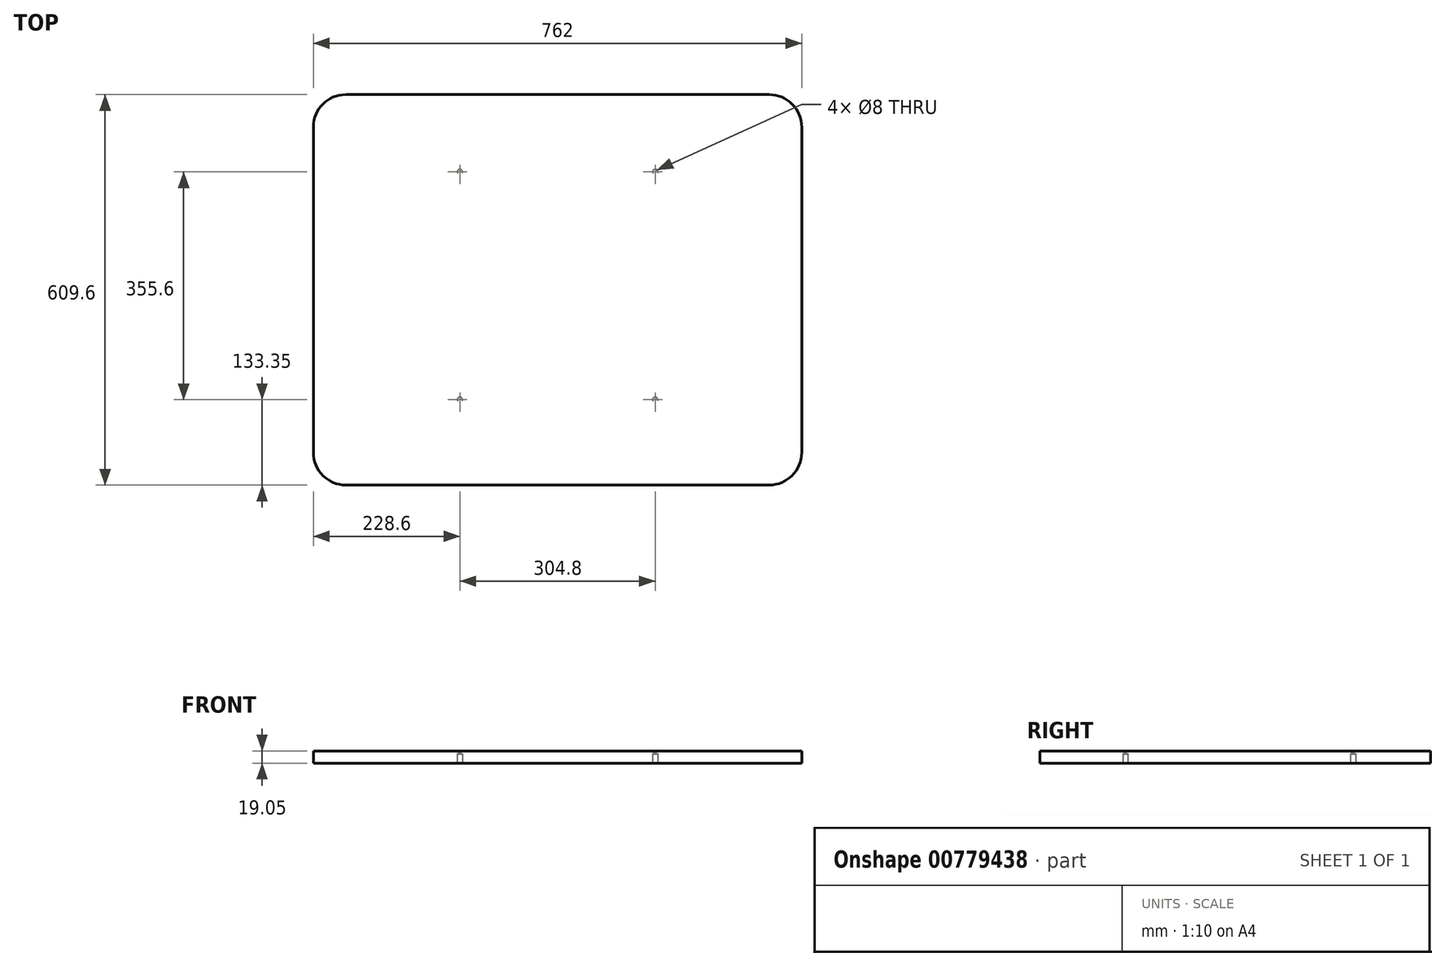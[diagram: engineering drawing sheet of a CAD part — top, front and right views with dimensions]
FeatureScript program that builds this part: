
annotation { "Feature Type Name" : "Feature", "Feature Type Description" : "" }
export const myFeature = defineFeature(function(context is Context, id is Id, definition is map)
    precondition{}
    {
        {
            var Q0;
            Q0=qCreatedBy(makeId("Top.planeOp"),FACE);
            var sketch = newSketch(context, id + "F0", { "sketchPlane" : qUnion([Q0])});
            skLineSegment(sketch, "E0.bottom", {"start": v(-330.2, 304.8) * mm, "end": v(330.2, 304.8) * mm});
            skLineSegment(sketch, "E0.top", {"start": v(-330.2, -304.8) * mm, "end": v(330.2, -304.8) * mm});
            skLineSegment(sketch, "E0.left", {"start": v(-381, 254) * mm, "end": v(-381, -254) * mm});
            skLineSegment(sketch, "E0.right", {"start": v(381, 254) * mm, "end": v(381, -254) * mm});
            skPoint(sketch, "E0.middle", {"position": v(0, 0) * mm});
            skPoint(sketch, "E1.visualSharp", {"position": v(-381, 304.8) * mm});
            skArc(sketch, "E1.filletArc", {"start": v(-330.2, 304.8) * mm, "mid": v(-366.12, 289.92) * mm, "end": v(-381, 254) * mm});
            skPoint(sketch, "E2.visualSharp", {"position": v(381, 304.8) * mm});
            skArc(sketch, "E2.filletArc", {"start": v(381, 254) * mm, "mid": v(366.12, 289.92) * mm, "end": v(330.2, 304.8) * mm});
            skPoint(sketch, "E3.visualSharp", {"position": v(381, -304.8) * mm});
            skArc(sketch, "E3.filletArc", {"start": v(330.2, -304.8) * mm, "mid": v(366.12, -289.92) * mm, "end": v(381, -254) * mm});
            skPoint(sketch, "E4.visualSharp", {"position": v(-381, -304.8) * mm});
            skArc(sketch, "E4.filletArc", {"start": v(-381, -254) * mm, "mid": v(-366.12, -289.92) * mm, "end": v(-330.2, -304.8) * mm});
            skSolve(sketch);
        }
        {
            var Q0;
            Q0=makeQuery(id+"F0.imprint","IMPRINT",FACE,{"disambiguationData":[TD([[makeQuery(id+"F0.imprint","IMPRINT",EDGE,{"derivedFrom":sQuery(id+"F0.wireOp",EDGE,"E0.bottom")}),-1.0]])]});
            extrude(context, id + "F1", {"entities" : qUnion([Q0]), "depth" : 19.05 * mm, "offsetDistance" : 25.4 * mm});
        }
        {
            var Q0;
            Q0=makeQuery(id+"F1.opExtrude","CAP_FACE",FACE,{"disambiguationData":[OSD([sQuery(id+"F0.wireOp",EDGE,"E0.bottom"),sQuery(id+"F0.wireOp",EDGE,"E0.top"),sQuery(id+"F0.wireOp",EDGE,"E0.left"),sQuery(id+"F0.wireOp",EDGE,"E0.right"),sQuery(id+"F0.wireOp",EDGE,"E1.filletArc"),sQuery(id+"F0.wireOp",EDGE,"E2.filletArc"),sQuery(id+"F0.wireOp",EDGE,"E3.filletArc"),sQuery(id+"F0.wireOp",EDGE,"E4.filletArc")])],"isStart":true});
            var sketch = newSketch(context, id + "F2", { "sketchPlane" : qUnion([Q0])});
            skLineSegment(sketch, "E5", {"start": v(0, -304.8) * mm, "end": v(0, -184.15) * mm});
            skLineSegment(sketch, "E6.bottom", {"start": v(0, -184.15) * mm, "end": v(152.4, -184.15) * mm});
            skLineSegment(sketch, "E6.top", {"start": v(0, 171.45) * mm, "end": v(152.4, 171.45) * mm});
            skLineSegment(sketch, "E6.left", {"start": v(0, -184.15) * mm, "end": v(0, 171.45) * mm});
            skLineSegment(sketch, "E6.right", {"start": v(152.4, -184.15) * mm, "end": v(152.4, 171.45) * mm});
            skLineSegment(sketch, "E7.bottom", {"start": v(0, -184.15) * mm, "end": v(-152.4, -184.15) * mm});
            skLineSegment(sketch, "E7.top", {"start": v(0, 171.45) * mm, "end": v(-152.4, 171.45) * mm});
            skLineSegment(sketch, "E7.right", {"start": v(-152.4, -184.15) * mm, "end": v(-152.4, 171.45) * mm});
            skPoint(sketch, "E8", {"position": v(-152.4, 171.45) * mm});
            skPoint(sketch, "E9", {"position": v(152.4, 171.45) * mm});
            skPoint(sketch, "E10", {"position": v(152.4, -184.15) * mm});
            skPoint(sketch, "E11", {"position": v(-152.4, -184.15) * mm});
            skSolve(sketch);
        }
        {
            var Q0;
            Q0=sQuery(id+"F2.wireOp",VERTEX,"E8");
            var Q1;
            Q1=sQuery(id+"F2.wireOp",VERTEX,"E9");
            var Q2;
            Q2=sQuery(id+"F2.wireOp",VERTEX,"E10");
            var Q3;
            Q3=sQuery(id+"F2.wireOp",VERTEX,"E11");
            var Q4;
            Q4=makeQuery(id+"F1.opExtrude","SWEPT_BODY",BODY,{"disambiguationData":[OSD([sQuery(id+"F0.wireOp",EDGE,"E0.bottom"),sQuery(id+"F0.wireOp",EDGE,"E0.top"),sQuery(id+"F0.wireOp",EDGE,"E0.left"),sQuery(id+"F0.wireOp",EDGE,"E0.right"),sQuery(id+"F0.wireOp",EDGE,"E1.filletArc"),sQuery(id+"F0.wireOp",EDGE,"E2.filletArc"),sQuery(id+"F0.wireOp",EDGE,"E3.filletArc"),sQuery(id+"F0.wireOp",EDGE,"E4.filletArc")])]});
            hole(context, id + "F3", {"style" : HoleStyle.SIMPLE, "endStyle" : HoleEndStyle.BLIND, "holeDiameter" : 8 * mm, "majorDiameter" : 6.35 * mm, "holeDepth" : 14.22 * mm, "isTappedThrough" : true, "tappedDepth" : 12.7 * mm, "tapClearance" : 3, "startFromSketch" : true, "locations" : qUnion([Q0, Q1, Q2, Q3]), "scope" : qUnion([Q4])});
        }
    });
